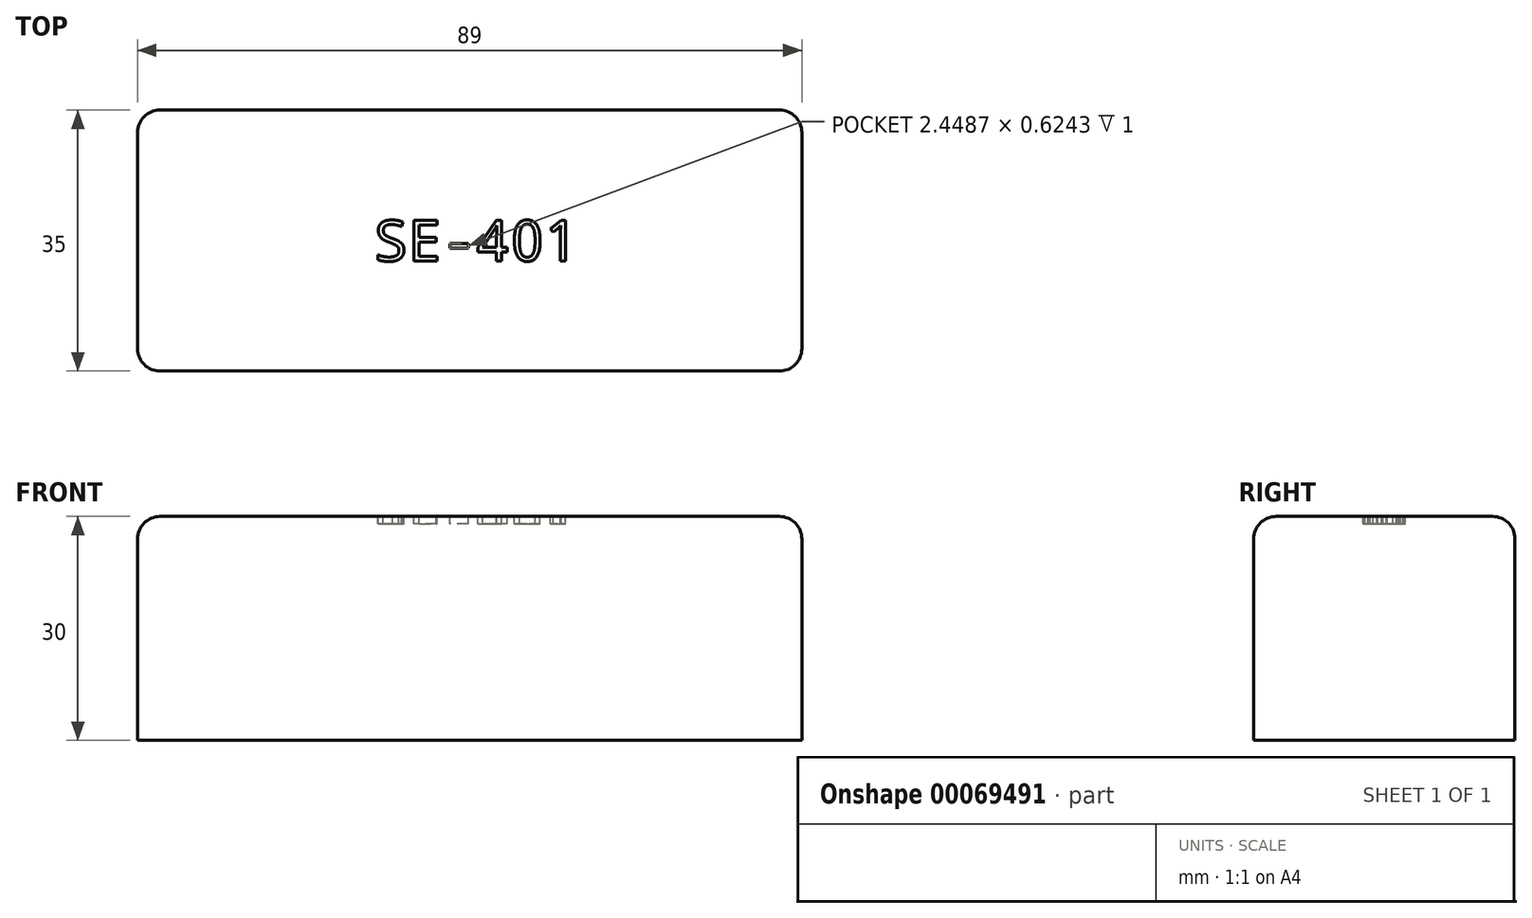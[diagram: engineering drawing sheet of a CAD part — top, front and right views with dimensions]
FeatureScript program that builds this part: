
annotation { "Feature Type Name" : "Feature", "Feature Type Description" : "" }
export const myFeature = defineFeature(function(context is Context, id is Id, definition is map)
    precondition{}
    {
        {
            var Q0;
            Q0=qCreatedBy(makeId("Top.planeOp"),FACE);
            var sketch = newSketch(context, id + "F0", { "sketchPlane" : qUnion([Q0])});
            skLineSegment(sketch, "E0.rect.bottom", {"start": v(-44.5, 17.5) * mm, "end": v(44.5, 17.5) * mm});
            skLineSegment(sketch, "E0.rect.top", {"start": v(-44.5, -17.5) * mm, "end": v(44.5, -17.5) * mm});
            skLineSegment(sketch, "E0.rect.left", {"start": v(-44.5, 17.5) * mm, "end": v(-44.5, -17.5) * mm});
            skLineSegment(sketch, "E0.rect.right", {"start": v(44.5, 17.5) * mm, "end": v(44.5, -17.5) * mm});
            skPoint(sketch, "E0.rect.middle", {"position": v(0, 0) * mm});
            skSolve(sketch);
        }
        {
            var Q0;
            Q0 = qSketchRegion(id + "F0", true);
            extrude(context, id + "F1", {"entities" : qUnion([Q0]), "endBound" : BoundingType.SYMMETRIC, "depth" : 30 * mm});
        }
        {
            var Q0;
            Q0=makeQuery(id+"F1.opExtrude","SWEPT_EDGE",EDGE,{"disambiguationData":[OSD([sQuery(id+"F0.wireOp",EDGE,"E0.rect.top"),sQuery(id+"F0.wireOp",EDGE,"E0.rect.left")])]});
            var Q1;
            Q1=makeQuery(id+"F1.opExtrude","SWEPT_EDGE",EDGE,{"disambiguationData":[OSD([sQuery(id+"F0.wireOp",EDGE,"E0.rect.top"),sQuery(id+"F0.wireOp",EDGE,"E0.rect.right")])]});
            var Q2;
            Q2=makeQuery(id+"F1.opExtrude","CAP_EDGE",EDGE,{"disambiguationData":[OSD([sQuery(id+"F0.wireOp",EDGE,"E0.rect.top")])],"isStart":false});
            var Q3;
            Q3=makeQuery(id+"F1.opExtrude","CAP_EDGE",EDGE,{"disambiguationData":[OSD([sQuery(id+"F0.wireOp",EDGE,"E0.rect.left")])],"isStart":false});
            var Q4;
            Q4=makeQuery(id+"F1.opExtrude","CAP_FACE",FACE,{"disambiguationData":[OSD([sQuery(id+"F0.wireOp",EDGE,"E0.rect.bottom"),sQuery(id+"F0.wireOp",EDGE,"E0.rect.top"),sQuery(id+"F0.wireOp",EDGE,"E0.rect.left"),sQuery(id+"F0.wireOp",EDGE,"E0.rect.right")])],"isStart":false});
            var Q5;
            Q5=makeQuery(id+"F1.opExtrude","SWEPT_EDGE",EDGE,{"disambiguationData":[OSD([sQuery(id+"F0.wireOp",EDGE,"E0.rect.bottom"),sQuery(id+"F0.wireOp",EDGE,"E0.rect.left")])]});
            var Q6;
            Q6=makeQuery(id+"F1.opExtrude","SWEPT_EDGE",EDGE,{"disambiguationData":[OSD([sQuery(id+"F0.wireOp",EDGE,"E0.rect.bottom"),sQuery(id+"F0.wireOp",EDGE,"E0.rect.right")])]});
            fillet(context, id + "F2", {"entities" : qUnion([Q0, Q1, Q2, Q3, Q4, Q5, Q6]), "radius" : 3 * mm, "tangentPropagation" : true, "allowEdgeOverflow" : false});
        }
        {
            var Q0;
            Q0=makeQuery(id+"F1.opExtrude","CAP_FACE",FACE,{"disambiguationData":[OSD([sQuery(id+"F0.wireOp",EDGE,"E0.rect.bottom"),sQuery(id+"F0.wireOp",EDGE,"E0.rect.top"),sQuery(id+"F0.wireOp",EDGE,"E0.rect.left"),sQuery(id+"F0.wireOp",EDGE,"E0.rect.right")])],"isStart":false});
            var sketch = newSketch(context, id + "F3", { "sketchPlane" : qUnion([Q0])});
            skText(sketch, "E1", { "text": "SE-401", "fontName": "DroidSansMono.ttf"});
            const initialGuessF3  = {"E1": [-0.01284, -0.00274, 1, 0, 0.00548]};
            skSetInitialGuess(sketch, initialGuessF3);
            skSolve(sketch);
        }
        {
            var Q0;
            Q0 = qSketchRegion(id + "F3", true);
            extrude(context, id + "F4", {"entities" : qUnion([Q0]), "operationType" : NewBodyOperationType.REMOVE, "oppositeDirection" : true, "depth" : 1 * mm});
        }
    });
